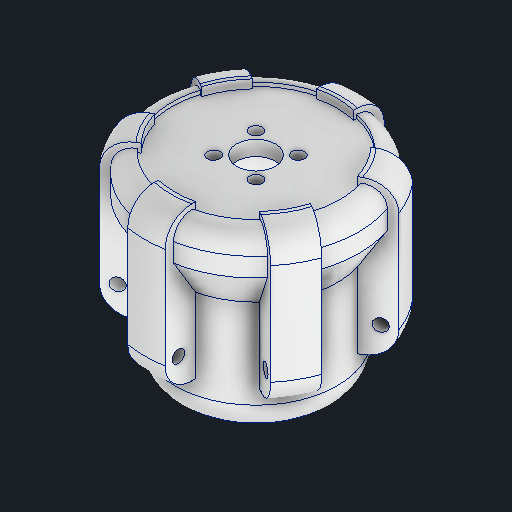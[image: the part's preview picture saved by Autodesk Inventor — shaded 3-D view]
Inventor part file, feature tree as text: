
AUTODESK INVENTOR PART (.ipt)
format: ipt  version: 2025.3 (Build 293356030, 356C)  size: 502,272 bytes
history: native  units: mm
features: sketch x7, extrude x3, fillet x3, pattern_circular x3, plane x2, hole x2, projected_geometry x2, revolve x1
ambient origin geometry x8: Origin, YZ Plane, XZ Plane, XY Plane, X Axis, Y Axis, Z Axis, Center Point
bodies: Solid2 (feature_tree)
feature tree (23):
  revolve  "Revolution2"  [1 undecoded]
  plane  "Work Plane1"
  extrude  "Extrusion1"  Depth=10.0mm
  plane  "Work Plane2"
  sketch  "Sketch7"  dims[d18=3.25mm]
  fillet  "Fillet2"  Radius=55.0mm
  pattern_circular  "Circular Pattern1"  [2 undecoded]
  fillet  "Fillet3"  Radius=7.0mm
  hole  "Hole2"  [1 undecoded]
  extrude  "Extrusión3"  Depth=7.0mm
  fillet  "Empalme4"  Radius=8.0mm
  pattern_circular  "Patrón circular2"  [2 undecoded]
  extrude  "Extrusión4"  Depth=7.0mm
  hole  "Agujero3"  [1 undecoded]
  pattern_circular  "Patrón circular3"  [2 undecoded]
  sketch  "Sketch4"  dims[d11=36.85mm d12=10.4mm]
  sketch  "Sketch5"  dims[d13=5.0mm d14=10.0mm d15=55.0mm]
  sketch  "Sketch8"  dims[d19=10.0mm]
  sketch  "Boceto10"  dims[d22=43.425mm]
  projected_geometry  "Contorno proyectado2"
  sketch  "Boceto11"  dims[d24=90.0deg]
  projected_geometry  "Contorno proyectado3"
  sketch  "Boceto12"  dims[d25=-24.682mm d29=15.0mm d30=0.0mm d41=7.0mm d42=60.0mm d43=360.0deg d45=3.0mm d48=8.0mm d50=5.0mm d51=11.314mm d52=3.4mm d53=6.0mm d54=6.3mm d55=2.0mm d56=90.0deg d57=8.0mm d58=20.594885mm d59=50.0mm d63=26.0mm d64=0.0mm d65=7.0mm d66=60.0mm d67=360.0deg d69=1.0mm d70=0.0mm d72=8.0mm d73=3.4mm d74=6.0mm d75=6.3mm d76=2.0mm d77=90.0deg d78=8.0mm d79=20.594885mm d80=60.0mm d81=360.0deg d83=25.74mm d60=20.594885mm d61=0.0625mm d62=0.75mm]
note: 9 required parameter values undecoded (feature->parameter linkage not recoverable at this tier; creation-order binding heuristic only, values carry confidence <= 0.55)